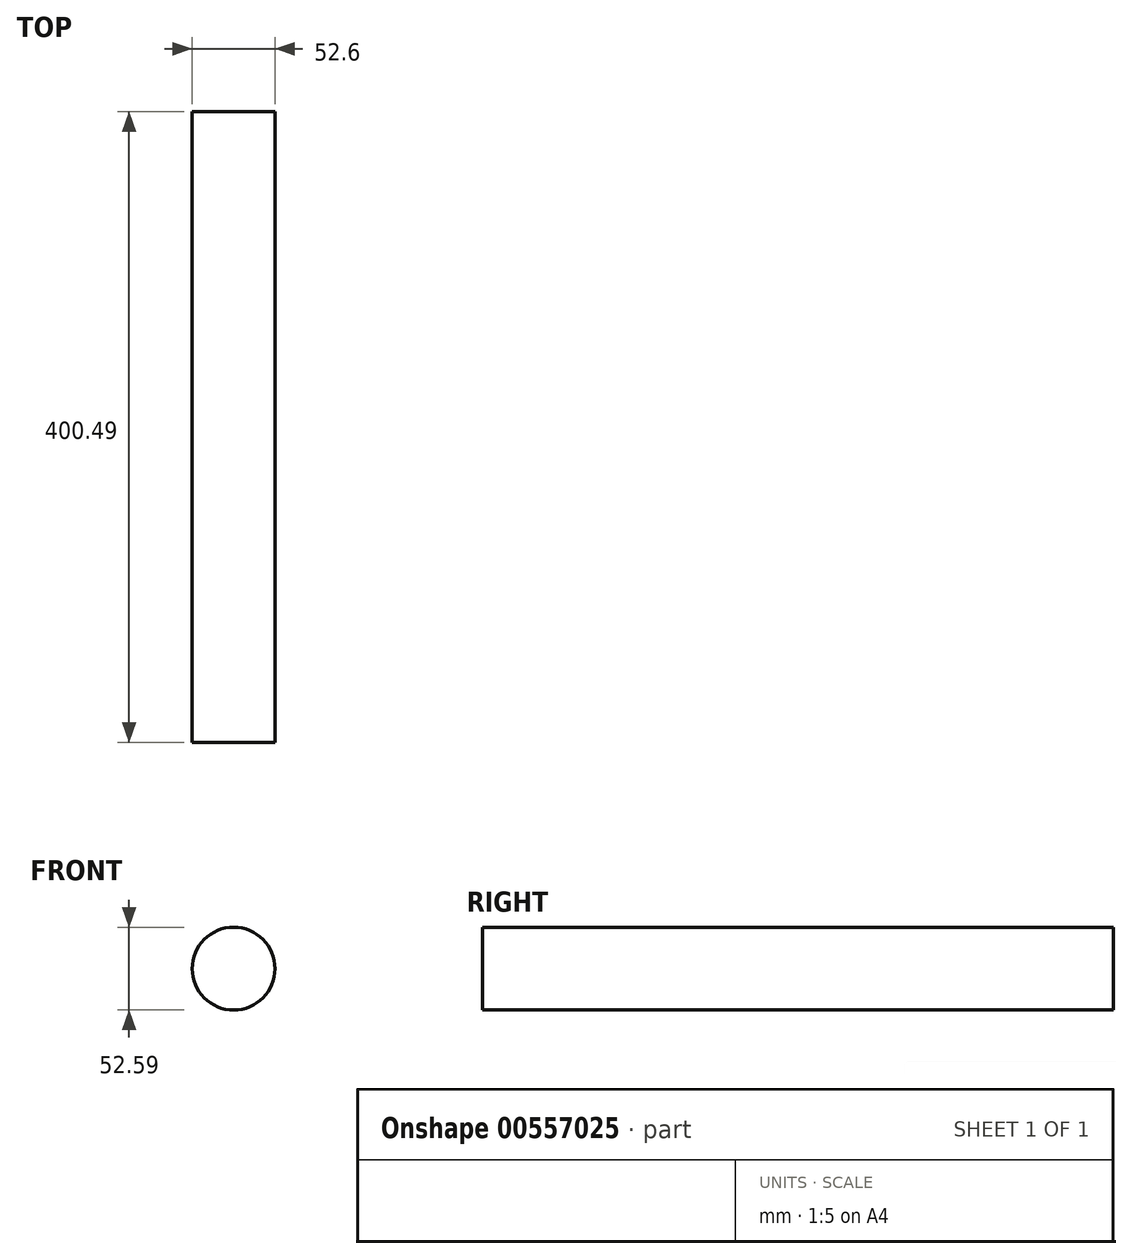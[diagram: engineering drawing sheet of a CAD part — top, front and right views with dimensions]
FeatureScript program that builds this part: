
annotation { "Feature Type Name" : "Feature", "Feature Type Description" : "" }
export const myFeature = defineFeature(function(context is Context, id is Id, definition is map)
    precondition{}
    {
        {
            var Q0;
            Q0=qCreatedBy(makeId("Front.planeOp"),FACE);
            var sketch = newSketch(context, id + "F0", { "sketchPlane" : qUnion([Q0])});
            skCircle(sketch, "E0", {"center": v(35.55, 42.14) * mm, "radius": 21.76 * mm});
            skCircle(sketch, "E1", {"center": v(35.55, 42.14) * mm, "radius": 26.3 * mm});
            skSolve(sketch);
        }
        {
            var Q0;
            Q0=makeQuery(id+"F0.imprint","IMPRINT",FACE,{"disambiguationData":[TD([[makeQuery(id+"F0.imprint","IMPRINT",EDGE,{"derivedFrom":sQuery(id+"F0.wireOp",EDGE,"E0")}),1.0]])]});
            var Q1;
            Q1=makeQuery(id+"F0.imprint","IMPRINT",FACE,{"disambiguationData":[TD([[makeQuery(id+"F0.imprint","IMPRINT",EDGE,{"derivedFrom":sQuery(id+"F0.wireOp",EDGE,"E0")}),-1.0]])]});
            extrude(context, id + "F1", {"entities" : qUnion([Q0, Q1]), "oppositeDirection" : true, "depth" : 25.4 * mm, "offsetDistance" : 25.4 * mm});
        }
        {
            var Q0;
            Q0=makeQuery(id+"F1.opExtrude","CAP_FACE",FACE,{"disambiguationData":[OSD([sQuery(id+"F0.wireOp",EDGE,"E1")])],"isStart":true});
            extrude(context, id + "F2", {"entities" : qUnion([Q0]), "operationType" : NewBodyOperationType.ADD, "depth" : 25.4 * mm, "offsetDistance" : 25.4 * mm});
        }
        {
            var Q0;
            Q0=makeQuery(id+"F2.opExtrude","CAP_FACE",FACE,{"disambiguationData":[OSD([sQuery(id+"F0.wireOp",EDGE,"E1")])],"isStart":false});
            extrude(context, id + "F3", {"entities" : qUnion([Q0]), "operationType" : NewBodyOperationType.ADD, "endBound" : BoundingType.THROUGH_ALL, "oppositeDirection" : true, "depth" : 25.4 * mm, "offsetDistance" : 25.4 * mm, "hasSecondDirection" : true, "secondDirectionBound" : SecondDirectionBoundingType.THROUGH_ALL, "secondDirectionOppositeDirection" : false, "secondDirectionDepth" : 25.4 * mm});
        }
        {
            var Q0;
            Q0=makeQuery(id+"F3.opExtrude","CAP_FACE",FACE,{"disambiguationData":[OSD([sQuery(id+"F0.wireOp",EDGE,"E1")])],"isStart":true});
            extrude(context, id + "F4", {"entities" : qUnion([Q0]), "operationType" : NewBodyOperationType.ADD, "endBound" : BoundingType.THROUGH_ALL, "depth" : 25.4 * mm, "offsetDistance" : 25.4 * mm, "hasSecondDirection" : true, "secondDirectionOppositeDirection" : true, "secondDirectionDepth" : 25.4 * mm});
        }
        {
            var Q0;
            Q0=makeQuery(id+"F4.opExtrude","CAP_FACE",FACE,{"disambiguationData":[OSD([sQuery(id+"F0.wireOp",EDGE,"E1")])],"isStart":false});
            extrude(context, id + "F5", {"entities" : qUnion([Q0]), "operationType" : NewBodyOperationType.ADD, "depth" : 25.4 * mm, "offsetDistance" : 25.4 * mm});
        }
    });
